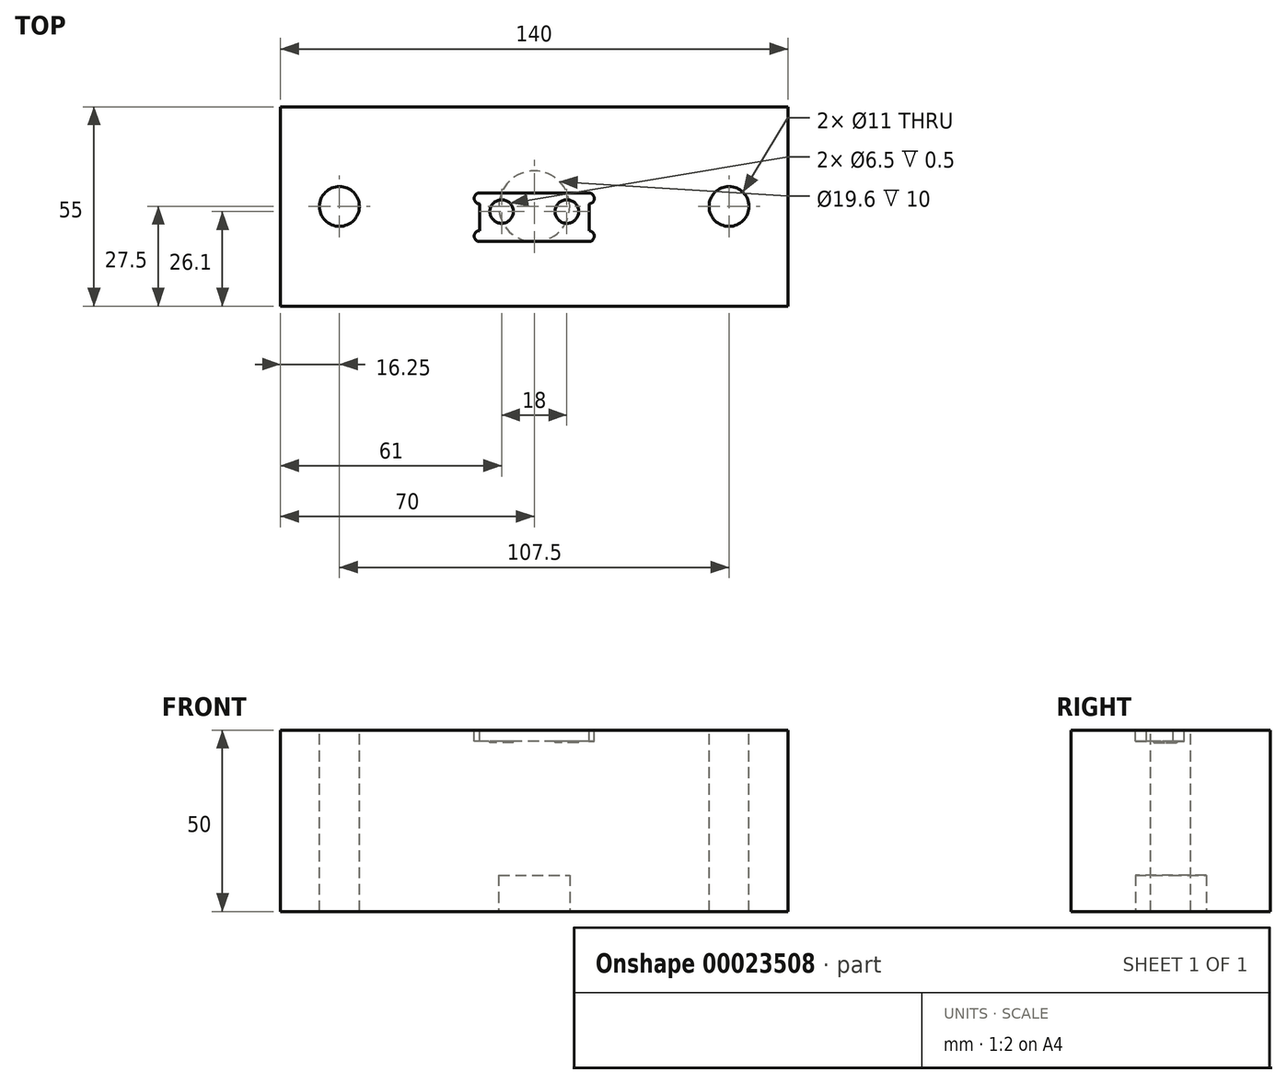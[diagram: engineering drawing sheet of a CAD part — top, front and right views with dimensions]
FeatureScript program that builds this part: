
annotation { "Feature Type Name" : "Feature", "Feature Type Description" : "" }
export const myFeature = defineFeature(function(context is Context, id is Id, definition is map)
    precondition{}
    {
        {
            var Q0;
            Q0=qCreatedBy(makeId("Front.planeOp"),FACE);
            var sketch = newSketch(context, id + "F0", { "sketchPlane" : qUnion([Q0])});
            skLineSegment(sketch, "E0.bottom", {"start": v(0, 0) * mm, "end": v(-140, 0) * mm});
            skLineSegment(sketch, "E0.top", {"start": v(0, 50) * mm, "end": v(-63.5, 50) * mm});
            skLineSegment(sketch, "E0.left", {"start": v(0, 0) * mm, "end": v(0, 50) * mm});
            skLineSegment(sketch, "E0.right", {"start": v(-140, 0) * mm, "end": v(-140, 50) * mm});
            skLineSegment(sketch, "E1.trimOffspring", {"start": v(-76.5, 50) * mm, "end": v(-140, 50) * mm});
            skPoint(sketch, "E2.center.orphan", {"position": v(-70, 50) * mm});
            skLineSegment(sketch, "E3", {"start": v(-63.5, 50) * mm, "end": v(-76.5, 50) * mm});
            skSolve(sketch);
        }
        {
            var Q0;
            Q0=makeQuery(id+"F0.imprint","IMPRINT",FACE,{"disambiguationData":[TD([[makeQuery(id+"F0.imprint","IMPRINT",EDGE,{"derivedFrom":sQuery(id+"F0.wireOp",EDGE,"E0.bottom")}),-1.0]])]});
            extrude(context, id + "F1", {"entities" : qUnion([Q0]), "depth" : 55 * mm});
        }
        {
            var Q0;
            Q0=makeQuery(id+"F1.opExtrude","SWEPT_FACE",FACE,{"disambiguationData":[OSD([sQuery(id+"F0.wireOp",EDGE,"E1.trimOffspring")])]});
            var sketch = newSketch(context, id + "F2", { "sketchPlane" : qUnion([Q0])});
            skCircle(sketch, "E4", {"center": v(-123.75, -27.5) * mm, "radius": 5.5 * mm});
            skCircle(sketch, "E5", {"center": v(-16.25, -27.5) * mm, "radius": 5.5 * mm});
            skSolve(sketch);
        }
        {
            var Q0;
            Q0=qSketchRegion(id+"F2",true);
            extrude(context, id + "F3", {"entities" : qUnion([Q0]), "operationType" : NewBodyOperationType.REMOVE, "endBound" : BoundingType.THROUGH_ALL, "oppositeDirection" : true, "depth" : 25 * mm});
        }
        {
            var Q0;
            Q0=makeQuery(id+"F1.opExtrude","SWEPT_FACE",FACE,{"disambiguationData":[OSD([sQuery(id+"F0.wireOp",EDGE,"E0.bottom")])]});
            var sketch = newSketch(context, id + "F4", { "sketchPlane" : qUnion([Q0])});
            skCircle(sketch, "E6", {"center": v(-70, 27.5) * mm, "radius": 9.8 * mm});
            skSolve(sketch);
        }
        {
            var Q0;
            Q0=qSketchRegion(id+"F4",true);
            extrude(context, id + "F5", {"entities" : qUnion([Q0]), "operationType" : NewBodyOperationType.REMOVE, "oppositeDirection" : true, "depth" : 10 * mm});
        }
        {
            var Q0;
            Q0=makeQuery(id+"F1.opExtrude","SWEPT_FACE",FACE,{"disambiguationData":[OSD([sQuery(id+"F0.wireOp",EDGE,"E0.top"),sQuery(id+"F0.wireOp",EDGE,"E1.trimOffspring"),sQuery(id+"F0.wireOp",EDGE,"E3")])]});
            var sketch = newSketch(context, id + "F6", { "sketchPlane" : qUnion([Q0])});
            skLineSegment(sketch, "E7", {"start": v(-70, 0) * mm, "end": v(-70, -55) * mm, "construction": true});
            skLineSegment(sketch, "E8.rect.bottom", {"start": v(-54.94, -37.2) * mm, "end": v(-85.06, -37.2) * mm});
            skLineSegment(sketch, "E8.rect.top", {"start": v(-54.94, -23.8) * mm, "end": v(-85.06, -23.8) * mm});
            skPoint(sketch, "E8.rect.middle", {"position": v(-70, -30.5) * mm});
            skArc(sketch, "E9", {"start": v(-85.06, -23.8) * mm, "mid": v(-86.56, -25.3) * mm, "end": v(-85.06, -26.8) * mm});
            skArc(sketch, "E10", {"start": v(-85.06, -34.2) * mm, "mid": v(-86.56, -35.7) * mm, "end": v(-85.06, -37.2) * mm});
            skArc(sketch, "E11", {"start": v(-54.86, -26.8) * mm, "mid": v(-53.44, -25.26) * mm, "end": v(-54.94, -23.8) * mm});
            skArc(sketch, "E12", {"start": v(-54.94, -37.2) * mm, "mid": v(-53.44, -35.74) * mm, "end": v(-54.86, -34.2) * mm});
            skLineSegment(sketch, "E13", {"start": v(-85.06, -26.8) * mm, "end": v(-85.06, -34.2) * mm});
            skLineSegment(sketch, "E14", {"start": v(-54.86, -26.8) * mm, "end": v(-54.86, -34.2) * mm});
            skSolve(sketch);
        }
        {
            var Q0;
            Q0 = qSketchRegion(id + "F6", true);
            extrude(context, id + "F7", {"entities" : qUnion([Q0]), "operationType" : NewBodyOperationType.REMOVE, "oppositeDirection" : true, "depth" : 3 * mm});
        }
        {
            var Q0;
            Q0=makeQuery(id+"F7.boolean.opBoolean","COPY",FACE,{"derivedFrom":makeQuery(id+"F7.opExtrude","CAP_FACE",FACE,{"disambiguationData":[OSD([sQuery(id+"F6.wireOp",EDGE,"E8.rect.bottom"),sQuery(id+"F6.wireOp",EDGE,"E8.rect.top"),sQuery(id+"F6.wireOp",EDGE,"E8.rect.left"),sQuery(id+"F6.wireOp",EDGE,"E8.rect.right")])],"isStart":false})});
            var sketch = newSketch(context, id + "F8", { "sketchPlane" : qUnion([Q0])});
            skCircle(sketch, "E15", {"center": v(-79, -28.9) * mm, "radius": 3.25 * mm});
            skCircle(sketch, "E16", {"center": v(-61, -28.9) * mm, "radius": 3.25 * mm});
            skLineSegment(sketch, "E17", {"start": v(-70, 8.56) * mm, "end": v(-70, -60) * mm, "construction": true});
            skSolve(sketch);
        }
        {
            var Q0;
            Q0 = qSketchRegion(id + "F8", true);
            extrude(context, id + "F9", {"entities" : qUnion([Q0]), "operationType" : NewBodyOperationType.REMOVE, "oppositeDirection" : true, "depth" : 0.5 * mm});
        }
    });
